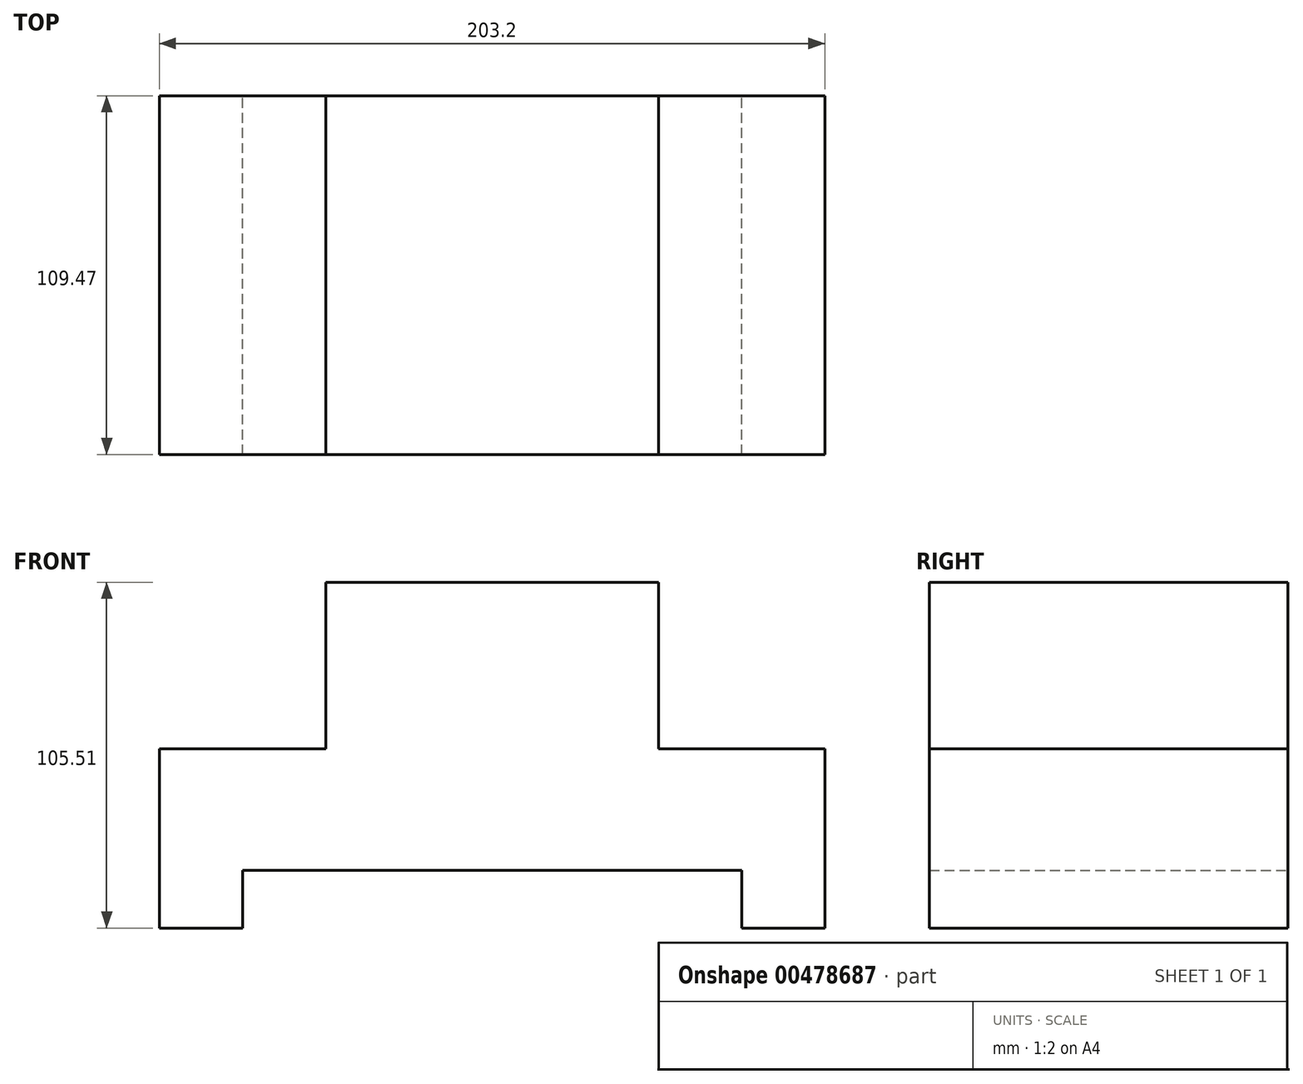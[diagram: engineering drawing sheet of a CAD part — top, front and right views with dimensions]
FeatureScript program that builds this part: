
annotation { "Feature Type Name" : "Feature", "Feature Type Description" : "" }
export const myFeature = defineFeature(function(context is Context, id is Id, definition is map)
    precondition{}
    {
        {
            var Q0;
            Q0=qCreatedBy(makeId("Front.planeOp"),FACE);
            var sketch = newSketch(context, id + "F0", { "sketchPlane" : qUnion([Q0])});
            skLineSegment(sketch, "E0", {"start": v(-106.18, -38.3) * mm, "end": v(-106.18, 16.42) * mm});
            skLineSegment(sketch, "E1", {"start": v(-106.18, 16.42) * mm, "end": v(-55.38, 16.42) * mm});
            skLineSegment(sketch, "E2", {"start": v(-55.38, 16.42) * mm, "end": v(-55.38, 67.22) * mm});
            skLineSegment(sketch, "E3", {"start": v(-55.38, 67.22) * mm, "end": v(46.22, 67.22) * mm});
            skLineSegment(sketch, "E4", {"start": v(46.22, 67.22) * mm, "end": v(46.22, 16.42) * mm});
            skLineSegment(sketch, "E5", {"start": v(46.22, 16.42) * mm, "end": v(97.02, 16.42) * mm});
            skLineSegment(sketch, "E6", {"start": v(97.02, 16.42) * mm, "end": v(97.02, -38.3) * mm});
            skLineSegment(sketch, "E7", {"start": v(97.02, -38.3) * mm, "end": v(71.62, -38.3) * mm});
            skLineSegment(sketch, "E8", {"start": v(71.62, -38.3) * mm, "end": v(71.62, -20.7) * mm});
            skLineSegment(sketch, "E9", {"start": v(71.62, -20.7) * mm, "end": v(-80.78, -20.7) * mm});
            skLineSegment(sketch, "E10", {"start": v(-80.78, -20.7) * mm, "end": v(-80.78, -38.3) * mm});
            skLineSegment(sketch, "E11", {"start": v(-80.78, -38.3) * mm, "end": v(-106.18, -38.3) * mm});
            skSolve(sketch);
        }
        {
            var Q0;
            Q0=makeQuery(id+"F0.imprint","IMPRINT",FACE,{"disambiguationData":[TD([[makeQuery(id+"F0.imprint","IMPRINT",EDGE,{"derivedFrom":sQuery(id+"F0.wireOp",EDGE,"E0")}),-1.0]])]});
            extrude(context, id + "F1", {"entities" : qUnion([Q0]), "depth" : 109.47 * mm});
        }
    });
